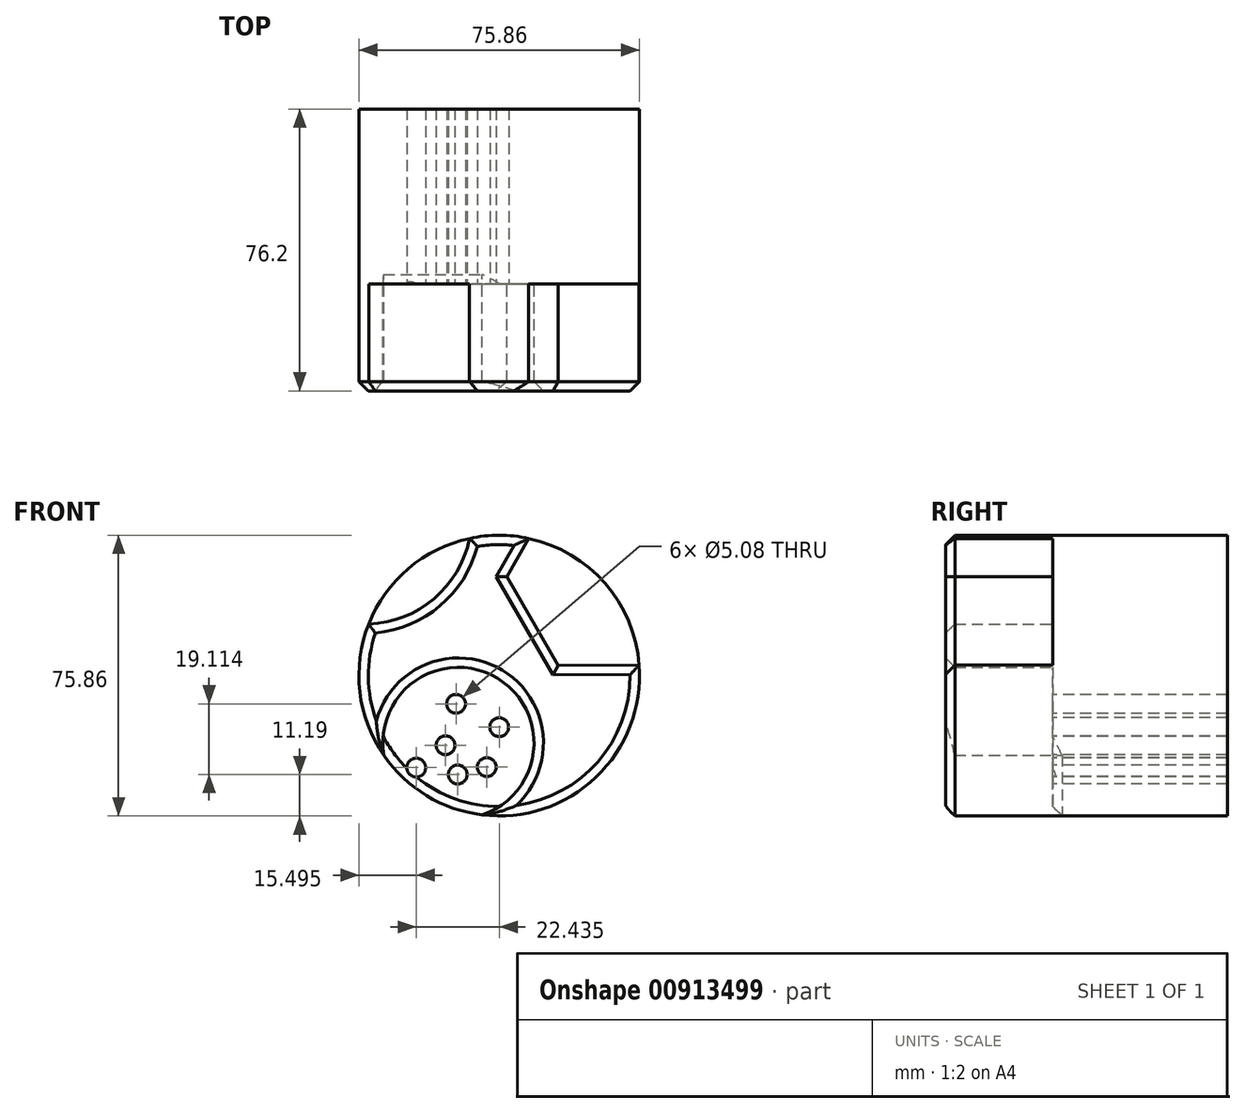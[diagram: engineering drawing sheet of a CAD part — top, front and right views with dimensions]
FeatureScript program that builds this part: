
annotation { "Feature Type Name" : "Feature", "Feature Type Description" : "" }
export const myFeature = defineFeature(function(context is Context, id is Id, definition is map)
    precondition{}
    {
        {
            var Q0;
            Q0=qCreatedBy(makeId("Front.planeOp"),FACE);
            var sketch = newSketch(context, id + "F0", { "sketchPlane" : qUnion([Q0])});
            skCircle(sketch, "E0", {"center": v(0, 0) * mm, "radius": 37.93 * mm});
            skSolve(sketch);
        }
        {
            var Q0;
            Q0=makeQuery(id+"F0.imprint","IMPRINT",FACE,{"disambiguationData":[TD([[makeQuery(id+"F0.imprint","IMPRINT",EDGE,{"derivedFrom":sQuery(id+"F0.wireOp",EDGE,"E0")}),1.0]])]});
            extrude(context, id + "F1", {"entities" : qUnion([Q0]), "depth" : 76.2 * mm, "offsetDistance" : 25.4 * mm});
        }
        {
            var Q0;
            Q0=qCreatedBy(makeId("Front.planeOp"),FACE);
            cPlane(context, id + "F2", {"entities" : qUnion([Q0]), "cplaneType" : CPlaneType.OFFSET, "offset" : 47.24 * mm, "width" : 152.4 * mm, "height" : 152.4 * mm});
        }
        {
            var Q0;
            Q0=qCreatedBy(id+"F2.planeOp",FACE);
            var sketch = newSketch(context, id + "F3", { "sketchPlane" : qUnion([Q0])});
            skLineSegment(sketch, "E1.bottom", {"start": v(-39.3, 52.08) * mm, "end": v(-7.42, 52.08) * mm});
            skLineSegment(sketch, "E1.top", {"start": v(-39.3, 13.89) * mm, "end": v(-36.44, 13.89) * mm});
            skLineSegment(sketch, "E1.left", {"start": v(-39.3, 52.08) * mm, "end": v(-39.3, 13.89) * mm});
            skLineSegment(sketch, "E1.right", {"start": v(-7.42, 52.08) * mm, "end": v(-7.42, 42.9) * mm});
            skPoint(sketch, "E2.visualSharp", {"position": v(-7.42, 13.89) * mm});
            skArc(sketch, "E2.filletArc", {"start": v(-36.44, 13.89) * mm, "mid": v(-15.92, 22.39) * mm, "end": v(-7.42, 42.9) * mm});
            skCircle(sketch, "E3.cCircle", {"center": v(29.83, 26.83) * mm, "radius": 24.04 * mm, "construction": true});
            skLineSegment(sketch, "E3.0", {"start": v(57.58, 26.86) * mm, "end": v(43.73, 2.8) * mm});
            skLineSegment(sketch, "E3.1", {"start": v(43.73, 2.8) * mm, "end": v(15.98, 2.77) * mm});
            skLineSegment(sketch, "E3.2", {"start": v(15.98, 2.77) * mm, "end": v(2.07, 26.8) * mm});
            skLineSegment(sketch, "E3.3", {"start": v(2.07, 26.8) * mm, "end": v(15.92, 50.85) * mm});
            skLineSegment(sketch, "E3.4", {"start": v(15.92, 50.85) * mm, "end": v(43.68, 50.88) * mm});
            skLineSegment(sketch, "E3.5", {"start": v(43.68, 50.88) * mm, "end": v(57.58, 26.86) * mm});
            skPoint(sketch, "E3.0.midPoint", {"position": v(50.66, 14.83) * mm});
            skCircle(sketch, "E4", {"center": v(-11.04, -18.22) * mm, "radius": 20.44 * mm});
            skSolve(sketch);
        }
        {
            var Q0;
            Q0=makeQuery(id+"F3.imprint","IMPRINT",FACE,{"disambiguationData":[TD([[makeQuery(id+"F3.imprint","IMPRINT",EDGE,{"derivedFrom":sQuery(id+"F3.wireOp",EDGE,"E1.bottom")}),-1.0]])]});
            var Q1;
            Q1=makeQuery(id+"F3.imprint","IMPRINT",FACE,{"disambiguationData":[TD([[makeQuery(id+"F3.imprint","IMPRINT",EDGE,{"derivedFrom":sQuery(id+"F3.wireOp",EDGE,"E3.0")}),-1.0]])]});
            var Q2;
            Q2=makeQuery(id+"F3.imprint","IMPRINT",FACE,{"disambiguationData":[TD([[makeQuery(id+"F3.imprint","IMPRINT",EDGE,{"derivedFrom":sQuery(id+"F3.wireOp",EDGE,"E4")}),1.0]])]});
            extrude(context, id + "F4", {"entities" : qUnion([Q0, Q1, Q2]), "operationType" : NewBodyOperationType.REMOVE, "depth" : 43.69 * mm, "offsetDistance" : 25.4 * mm});
        }
        {
            var Q0;
            Q0=makeQuery(id+"F1.opExtrude","CAP_FACE",FACE,{"disambiguationData":[OSD([sQuery(id+"F0.wireOp",EDGE,"E0")])],"isStart":false});
            chamfer(context, id + "F5", {"entities" : qUnion([Q0]), "width" : 2.54 * mm, "tangentPropagation" : true});
        }
        {
            var Q0;
            Q0=makeQuery(id+"F4.boolean.opBoolean","COPY",FACE,{"derivedFrom":makeQuery(id+"F4.opExtrude","CAP_FACE",FACE,{"disambiguationData":[OSD([sQuery(id+"F3.wireOp",EDGE,"E4")])],"isStart":true})});
            var sketch = newSketch(context, id + "F6", { "sketchPlane" : qUnion([Q0])});
            skPoint(sketch, "E5", {"position": v(-11.67, -7.63) * mm});
            skPoint(sketch, "E6", {"position": v(-14.53, -18.85) * mm});
            skPoint(sketch, "E7", {"position": v(0, -13.93) * mm});
            skPoint(sketch, "E8", {"position": v(-3.36, -24.74) * mm});
            skPoint(sketch, "E9", {"position": v(-11.2, -26.74) * mm});
            skPoint(sketch, "E10", {"position": v(-22.44, -24.87) * mm});
            skSolve(sketch);
        }
        {
            var Q0;
            Q0=sQuery(id+"F6.wireOp",VERTEX,"E5");
            var Q1;
            Q1=sQuery(id+"F6.wireOp",VERTEX,"E7");
            var Q2;
            Q2=sQuery(id+"F6.wireOp",VERTEX,"E6");
            var Q3;
            Q3=sQuery(id+"F6.wireOp",VERTEX,"E8");
            var Q4;
            Q4=sQuery(id+"F6.wireOp",VERTEX,"E9");
            var Q5;
            Q5=sQuery(id+"F6.wireOp",VERTEX,"E10");
            var Q6;
            Q6=makeQuery(id+"F1.opExtrude","SWEPT_BODY",BODY,{"disambiguationData":[OSD([sQuery(id+"F0.wireOp",EDGE,"E0")])]});
            hole(context, id + "F7", {"style" : HoleStyle.SIMPLE, "endStyle" : HoleEndStyle.THROUGH, "holeDiameter" : 5.08 * mm, "majorDiameter" : 6.35 * mm, "isTappedThrough" : true, "tappedDepth" : 12.7 * mm, "tapClearance" : 3, "locations" : qUnion([Q0, Q1, Q2, Q3, Q4, Q5]), "scope" : qUnion([Q6])});
        }
        {
            var Q0;
            Q0=makeQuery(id+"F4.boolean.opBoolean","INTERSECT",EDGE,{"derivedFrom":[makeQuery(id+"F1.opExtrude","SWEPT_FACE",FACE,{"disambiguationData":[OSD([sQuery(id+"F0.wireOp",EDGE,"E0")])]}),makeQuery(id+"F4.opExtrude","CAP_FACE",FACE,{"disambiguationData":[OSD([sQuery(id+"F3.wireOp",EDGE,"E4")])],"isStart":true})]});
            chamfer(context, id + "F8", {"entities" : qUnion([Q0]), "width" : 2.54 * mm, "tangentPropagation" : true});
        }
    });
